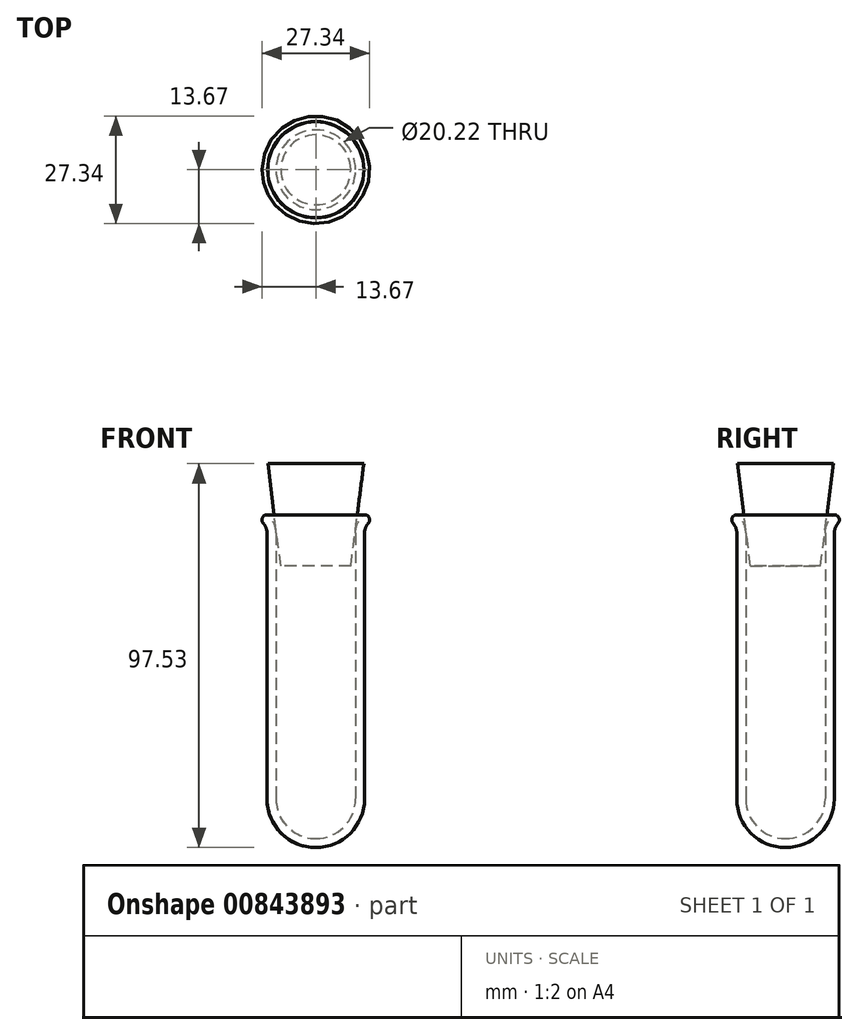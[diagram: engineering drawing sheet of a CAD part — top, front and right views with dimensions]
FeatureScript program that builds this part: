
annotation { "Feature Type Name" : "Feature", "Feature Type Description" : "" }
export const myFeature = defineFeature(function(context is Context, id is Id, definition is map)
    precondition{}
    {
        {
            var Q0;
            Q0=qCreatedBy(makeId("Front.planeOp"),FACE);
            var sketch = newSketch(context, id + "F0", { "sketchPlane" : qUnion([Q0])});
            skLineSegment(sketch, "E0", {"start": v(0, 0) * mm, "end": v(0, 84.53) * mm});
            skLineSegment(sketch, "E1", {"start": v(0, 84.53) * mm, "end": v(12.4, 84.53) * mm});
            skArc(sketch, "E2", {"start": v(13.35, 82.42) * mm, "mid": v(13.55, 83.79) * mm, "end": v(12.4, 84.53) * mm});
            skLineSegment(sketch, "E3", {"start": v(12.4, 79.9) * mm, "end": v(12.4, 12.4) * mm});
            skArc(sketch, "E4", {"start": v(0, 0) * mm, "mid": v(8.76, 3.63) * mm, "end": v(12.4, 12.4) * mm});
            skPoint(sketch, "E5.visualSharp", {"position": v(12.4, 82) * mm});
            skArc(sketch, "E5.filletArc", {"start": v(13.35, 82.42) * mm, "mid": v(12.64, 81.25) * mm, "end": v(12.4, 79.9) * mm});
            skSolve(sketch);
        }
        {
            var Q0;
            Q0=makeQuery(id+"F0.imprint","IMPRINT",FACE,{"disambiguationData":[TD([[makeQuery(id+"F0.imprint","IMPRINT",EDGE,{"derivedFrom":sQuery(id+"F0.wireOp",EDGE,"E0")}),-1.0]])]});
            var Q1;
            Q1=sQuery(id+"F0.wireOp",EDGE,"E0");
            revolve(context, id + "F1", {"surfaceOperationType" : NewSurfaceOperationType.NEW, "entities" : qUnion([Q0]), "axis" : qUnion([Q1]), "revolveType" : RevolveType.FULL});
        }
        {
            var Q0;
            Q0=makeQuery(id+"F1.opRevolve","SWEPT_FACE",FACE,{"disambiguationData":[OSD([sQuery(id+"F0.wireOp",EDGE,"E1")])]});
            shell(context, id + "F2", {"entities" : qUnion([Q0]), "thickness" : 2.3 * mm});
        }
        {
            var Q0;
            Q0=qCreatedBy(makeId("Front.planeOp"),FACE);
            var sketch = newSketch(context, id + "F3", { "sketchPlane" : qUnion([Q0])});
            skLineSegment(sketch, "E6", {"start": v(0, 71.53) * mm, "end": v(-8.9, 71.53) * mm});
            skLineSegment(sketch, "E7", {"start": v(-8.9, 71.53) * mm, "end": v(-12.2, 97.53) * mm});
            skLineSegment(sketch, "E8", {"start": v(-12.2, 97.53) * mm, "end": v(0, 97.53) * mm});
            skLineSegment(sketch, "E9", {"start": v(0, 97.53) * mm, "end": v(0, 71.53) * mm});
            skSolve(sketch);
        }
        {
            var Q0;
            Q0=makeQuery(id+"F3.imprint","IMPRINT",FACE,{"disambiguationData":[TD([[makeQuery(id+"F3.imprint","IMPRINT",EDGE,{"derivedFrom":sQuery(id+"F3.wireOp",EDGE,"E6")}),-1.0]])]});
            var Q1;
            Q1=sQuery(id+"F3.wireOp",EDGE,"E9");
            revolve(context, id + "F4", {"operationType" : NewBodyOperationType.ADD, "surfaceOperationType" : NewSurfaceOperationType.NEW, "entities" : qUnion([Q0]), "axis" : qUnion([Q1]), "revolveType" : RevolveType.FULL});
        }
    });
